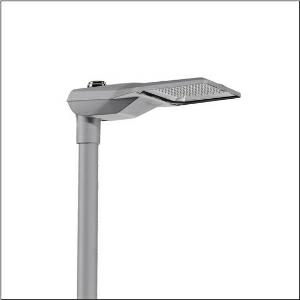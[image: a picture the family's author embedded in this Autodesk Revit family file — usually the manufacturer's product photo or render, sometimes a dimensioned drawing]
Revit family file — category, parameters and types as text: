
# Revit family: streetlight_sl_21_midi___p0_8a_5xe7u47n08lb_d940
name_source: partatom
category: Lighting Fixtures
units: mm (PartAtom-declared; Revit-internal decimal feet)

## family parameters
Cut with Voids When Loaded = No
Host = Face
Light Source = No
Part Type = Normal
Room Calculation Point = No
Round Connector Dimension = Use Diameter
Shared = No

## types (1)
- --- (1 x LED, 15080 lm, 98.3 W, 4000K)
    Apparent Load = 98 VA
    CIE Flux Codes = 33 69 96 100 100
    Color Rendering = 70
    Color Temperature = 4000K
    Default Elevation = 1800 mm
    Description = Streetlight SL 21 midi, mast luminaire, primary light control with lens, of PMMA, primary optical cover: cover, of toughened safety glass, transparent, light distribution: P0.8a, light emission: direct distribution, primary light characteristic: asymmetric, installation type: side-entry, LED, 3G 2.5mm², High Power LED, rated luminous flux: 15.080lm, luminous efficacy: 153lm/W, light colour: 740, colour temperature: 4000K, control gear: NEMA (7pin), control: flexible luminous flux parameterisation, time-dependent luminous flux control, constant luminous flux control, pre-setting: linear dimming characteristic, overheat protection, mains connection: 220..240V, AC, 50/60Hz, connection cable pre-assembled, cable length: 10,5m, wiring characteristics: H05VV-F, start of lifetime: 98W, end of service life: 101W, reduction: 45W, luminaire housing, of diecast aluminium (EN AC-44300), powder-coated, Siteco® metallic grey (DB 702S), corrosivity category C5 mid according to DIN EN ISO 12944, multi-level sealing system, sealing non-destructively replaceable, inclination adjustable: 0°, 5°, 10°, 15°, length: 644mm, width: 335mm, height: 110mm, spigot size: 42mm (side-entry), mounting height: 4..8m, protection rating (complete): IP66, insulation class (complete): insulation class I (protective earthing), certification: CE, ENEC, ENEC+, VDE, impact resistance: IK10, permissible operating ambient temperature for outdoor applications: -40..+50°C, standard-compliant lighting for roads and squares, packaging unit: 1 piece

Light Distribution: P0.8a
    Height = 111 mm
    Lamp = 1 x LED
    Lamp Light Flux = 15080 lm
    Lamp Power = 98.3 W
    Lamp count = 1
    Length = 644 mm
    Luminous efficacy = 153 lm/W
    Manufacturer = Siteco
    ModVariant = No
    Model = 5XE7U47N08LB
    Number of Poles = 1
    OnlyDefault = Yes
    Power Factor = 1
    Product Name = Streetlight SL 21 midi | P0.8a
    Product group = mast luminaire | pylon top
    ProductGroupID = 6100
    Protection Class = Protection class I
    Protection Degree = IP 66
    RLX_Detail_Level = 1
    RLX_Emergency_Light_Flux = 0 lm
    RLX_Emergency_Type = 0
    RLX_Emergency_Type_DB = No
    RlxData = <blob elided: 26477 chars, md5=05bf36cf>
    Socket = socket
    Standby Power = 0 W
    System Light Flux = 15080 lm
    System Power = 98 W
    Type Comments = factory setting: luminous flux: 100 % | dim-lin: 254 | 1020 mA
    Type Image = l_1294377.jpg
    URL = http://relux.com
    VarID = @adj_073268
    Voltage = 0 V
    Weight = 0.00 kg
    Width = 336 mm

## geometry (parser evidence)
native form markers: Blend x4, Sweep x11
no freeform markers — native parametric forms only
